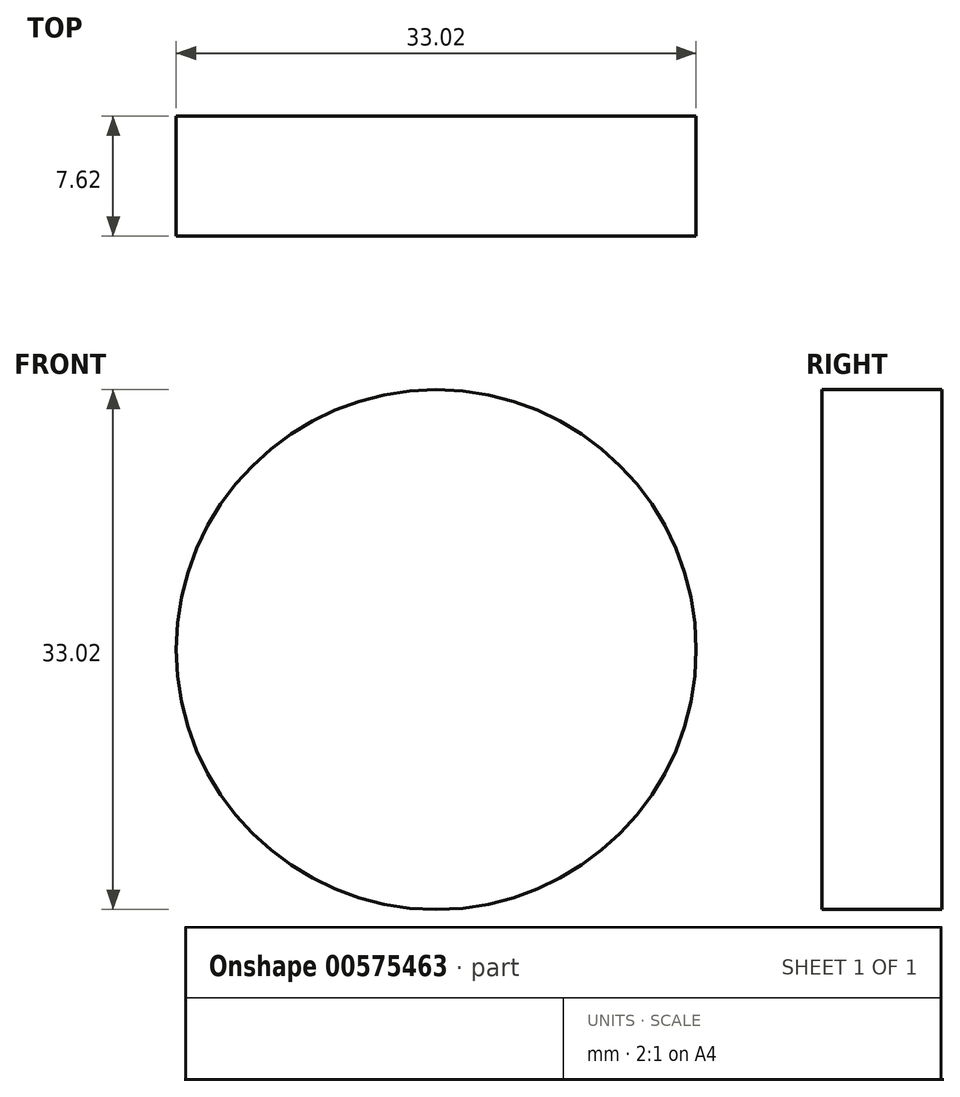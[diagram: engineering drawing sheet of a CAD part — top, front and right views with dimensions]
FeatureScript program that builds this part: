
annotation { "Feature Type Name" : "Feature", "Feature Type Description" : "" }
export const myFeature = defineFeature(function(context is Context, id is Id, definition is map)
    precondition{}
    {
        {
            var Q0;
            Q0=qCreatedBy(makeId("Front.planeOp"),FACE);
            var sketch = newSketch(context, id + "F0", { "sketchPlane" : qUnion([Q0])});
            skCircle(sketch, "E0", {"center": v(-36.12, 31.49) * mm, "radius": 16.51 * mm});
            skSolve(sketch);
        }
        {
            var Q0;
            Q0 = qSketchRegion(id + "F0", true);
            extrude(context, id + "F1", {"entities" : qUnion([Q0]), "depth" : 7.62 * mm, "offsetDistance" : 25.4 * mm});
        }
    });
